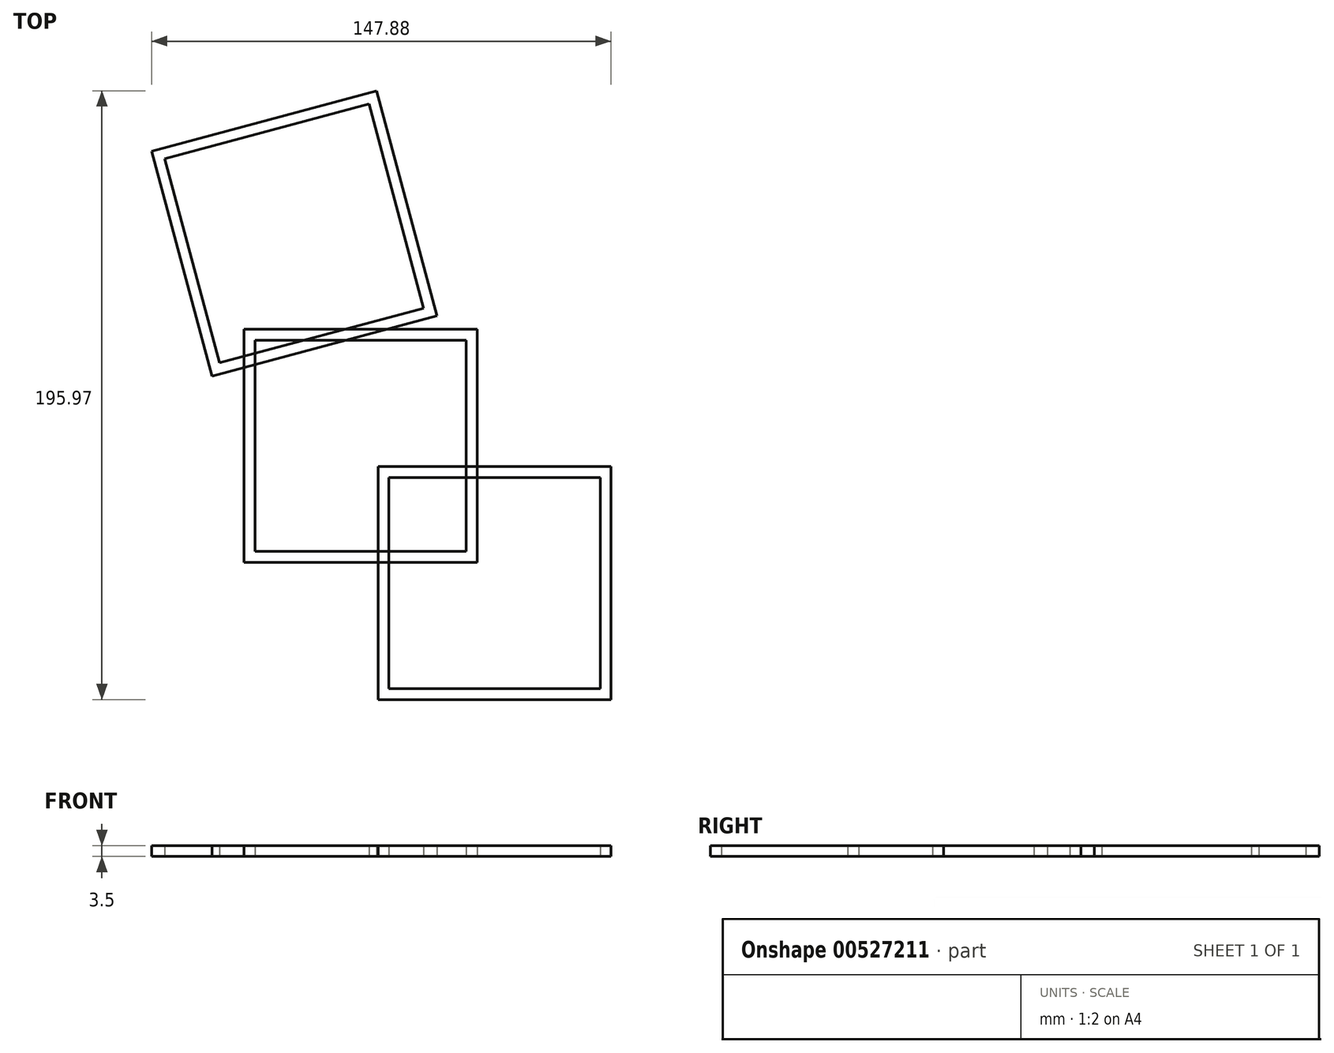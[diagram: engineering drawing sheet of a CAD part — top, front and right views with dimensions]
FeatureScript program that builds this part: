
annotation { "Feature Type Name" : "Feature", "Feature Type Description" : "" }
export const myFeature = defineFeature(function(context is Context, id is Id, definition is map)
    precondition{}
    {
        {
            var Q0;
            Q0=qCreatedBy(makeId("Top.planeOp"),FACE);
            var sketch = newSketch(context, id + "F0", { "sketchPlane" : qUnion([Q0])});
            skLineSegment(sketch, "E0.bottom", {"start": v(-53.67, 33.08) * mm, "end": v(21.33, 33.08) * mm});
            skLineSegment(sketch, "E0.top", {"start": v(-53.67, -41.92) * mm, "end": v(21.33, -41.92) * mm});
            skLineSegment(sketch, "E0.left", {"start": v(-53.67, 33.08) * mm, "end": v(-53.67, -41.92) * mm});
            skLineSegment(sketch, "E0.right", {"start": v(21.33, 33.08) * mm, "end": v(21.33, -41.92) * mm});
            skLineSegment(sketch, "E1.0", {"start": v(-50.17, 29.58) * mm, "end": v(17.83, 29.58) * mm});
            skLineSegment(sketch, "E1.1", {"start": v(-50.17, 29.58) * mm, "end": v(-50.17, -38.42) * mm});
            skLineSegment(sketch, "E1.2", {"start": v(-50.17, -38.42) * mm, "end": v(17.83, -38.42) * mm});
            skLineSegment(sketch, "E1.3", {"start": v(17.83, 29.58) * mm, "end": v(17.83, -38.42) * mm});
            skSolve(sketch);
        }
        {
            var Q0;
            Q0=makeQuery(id+"F0.imprint","IMPRINT",FACE,{"disambiguationData":[TD([[makeQuery(id+"F0.imprint","IMPRINT",EDGE,{"derivedFrom":sQuery(id+"F0.wireOp",EDGE,"E0.bottom")}),-1.0]])]});
            extrude(context, id + "F1", {"entities" : qUnion([Q0]), "depth" : 3.5 * mm, "offsetDistance" : 25 * mm});
        }
        {
            var Q0;
            Q0=makeQuery(id+"F1.opExtrude","SWEPT_BODY",BODY,{"disambiguationData":[OSD([sQuery(id+"F0.wireOp",EDGE,"E0.bottom"),sQuery(id+"F0.wireOp",EDGE,"E0.top"),sQuery(id+"F0.wireOp",EDGE,"E0.left"),sQuery(id+"F0.wireOp",EDGE,"E0.right"),sQuery(id+"F0.wireOp",EDGE,"E1.0"),sQuery(id+"F0.wireOp",EDGE,"E1.1"),sQuery(id+"F0.wireOp",EDGE,"E1.2"),sQuery(id+"F0.wireOp",EDGE,"E1.3")])]});
            var Q1;
            Q1=makeQuery(id+"F1.opExtrude","SWEPT_EDGE",EDGE,{"disambiguationData":[OSD([sQuery(id+"F0.wireOp",EDGE,"E0.top"),sQuery(id+"F0.wireOp",EDGE,"E0.left")])]});
            transform(context, id + "F2", {"entities" : qUnion([Q0]), "transformType" : TransformType.TRANSLATION_3D, "dx" : 43.1 * mm, "dy" : -44.2 * mm, "dz" : 0 * mm, "makeCopy" : true});
        }
        {
            var Q0;
            Q0=makeQuery(id+"F1.opExtrude","SWEPT_BODY",BODY,{"disambiguationData":[OSD([sQuery(id+"F0.wireOp",EDGE,"E0.bottom"),sQuery(id+"F0.wireOp",EDGE,"E0.top"),sQuery(id+"F0.wireOp",EDGE,"E0.left"),sQuery(id+"F0.wireOp",EDGE,"E0.right"),sQuery(id+"F0.wireOp",EDGE,"E1.0"),sQuery(id+"F0.wireOp",EDGE,"E1.1"),sQuery(id+"F0.wireOp",EDGE,"E1.2"),sQuery(id+"F0.wireOp",EDGE,"E1.3")])]});
            var Q1;
            Q1=makeQuery(id+"F1.opExtrude","SWEPT_EDGE",EDGE,{"disambiguationData":[OSD([sQuery(id+"F0.wireOp",EDGE,"E0.top"),sQuery(id+"F0.wireOp",EDGE,"E0.left")])]});
            var Q2;
            Q2=makeQuery(id+"F1.opExtrude","SWEPT_EDGE",EDGE,{"disambiguationData":[OSD([sQuery(id+"F0.wireOp",EDGE,"E1.0"),sQuery(id+"F0.wireOp",EDGE,"E1.1")])]});
            transform(context, id + "F3", {"entities" : qUnion([Q0]), "transformType" : TransformType.ROTATION, "transformAxis" : qUnion([Q2]), "angle" : 105 * degree, "oppositeDirection" : true, "makeCopy" : true});
        }
        {
            var Q0;
            Q0=makeQuery(id+"F3.opPattern","COPY",BODY,{"derivedFrom":makeQuery(id+"F1.opExtrude","SWEPT_BODY",BODY,{"disambiguationData":[OSD([sQuery(id+"F0.wireOp",EDGE,"E0.bottom"),sQuery(id+"F0.wireOp",EDGE,"E0.top"),sQuery(id+"F0.wireOp",EDGE,"E0.left"),sQuery(id+"F0.wireOp",EDGE,"E0.right"),sQuery(id+"F0.wireOp",EDGE,"E1.0"),sQuery(id+"F0.wireOp",EDGE,"E1.1"),sQuery(id+"F0.wireOp",EDGE,"E1.2"),sQuery(id+"F0.wireOp",EDGE,"E1.3")])]}),"instanceName":"1"});
            transform(context, id + "F4", {"entities" : qUnion([Q0]), "transformType" : TransformType.TRANSLATION_3D, "dx" : -11.4 * mm, "dy" : -7.3 * mm, "dz" : 0 * mm, "makeCopy" : false});
        }
        {
            var Q0;
            Q0=makeQuery(id+"F3.opPattern","COPY",BODY,{"derivedFrom":makeQuery(id+"F1.opExtrude","SWEPT_BODY",BODY,{"disambiguationData":[OSD([sQuery(id+"F0.wireOp",EDGE,"E0.bottom"),sQuery(id+"F0.wireOp",EDGE,"E0.top"),sQuery(id+"F0.wireOp",EDGE,"E0.left"),sQuery(id+"F0.wireOp",EDGE,"E0.right"),sQuery(id+"F0.wireOp",EDGE,"E1.0"),sQuery(id+"F0.wireOp",EDGE,"E1.1"),sQuery(id+"F0.wireOp",EDGE,"E1.2"),sQuery(id+"F0.wireOp",EDGE,"E1.3")])]}),"instanceName":"1"});
            var Q1;
            Q1=makeQuery(id+"F3.opPattern","COPY",EDGE,{"derivedFrom":makeQuery(id+"F1.opExtrude","SWEPT_EDGE",EDGE,{"disambiguationData":[OSD([sQuery(id+"F0.wireOp",EDGE,"E0.bottom"),sQuery(id+"F0.wireOp",EDGE,"E0.right")])]}),"instanceName":"1"});
            transform(context, id + "F5", {"entities" : qUnion([Q0]), "transformType" : TransformType.ROTATION, "transformAxis" : qUnion([Q1]), "angle" : 50 * degree, "oppositeDirection" : true, "makeCopy" : true});
        }
        {
            var Q0;
            Q0=makeQuery(id+"F5.opPattern","COPY",BODY,{"derivedFrom":makeQuery(id+"F3.opPattern","COPY",BODY,{"derivedFrom":makeQuery(id+"F1.opExtrude","SWEPT_BODY",BODY,{"disambiguationData":[OSD([sQuery(id+"F0.wireOp",EDGE,"E0.bottom"),sQuery(id+"F0.wireOp",EDGE,"E0.top"),sQuery(id+"F0.wireOp",EDGE,"E0.left"),sQuery(id+"F0.wireOp",EDGE,"E0.right"),sQuery(id+"F0.wireOp",EDGE,"E1.0"),sQuery(id+"F0.wireOp",EDGE,"E1.1"),sQuery(id+"F0.wireOp",EDGE,"E1.2"),sQuery(id+"F0.wireOp",EDGE,"E1.3")])]}),"instanceName":"1"}),"instanceName":"1"});
            deleteBodies(context, id + "F6", {"entities" : qUnion([Q0])});
        }
    });
